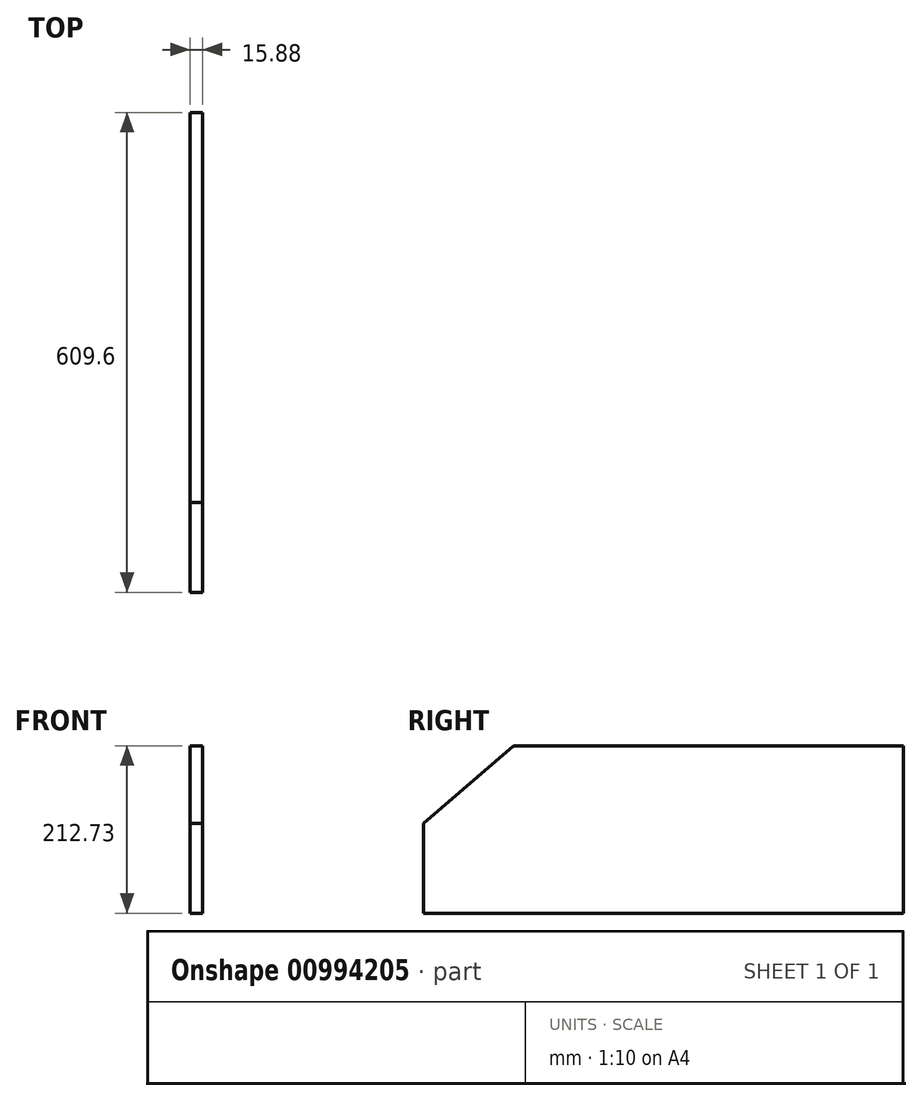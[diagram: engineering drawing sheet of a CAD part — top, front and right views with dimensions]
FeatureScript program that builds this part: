
annotation { "Feature Type Name" : "Feature", "Feature Type Description" : "" }
export const myFeature = defineFeature(function(context is Context, id is Id, definition is map)
    precondition{}
    {
        {
            var Q0;
            Q0=qCreatedBy(makeId("Right.planeOp"),FACE);
            var sketch = newSketch(context, id + "F0", { "sketchPlane" : qUnion([Q0])});
            skLineSegment(sketch, "E0", {"start": v(0.04, 0.07) * mm, "end": v(609.64, 0.07) * mm});
            skLineSegment(sketch, "E1", {"start": v(609.64, 0.07) * mm, "end": v(609.64, 212.8) * mm});
            skLineSegment(sketch, "E2", {"start": v(609.64, 212.8) * mm, "end": v(114.34, 212.8) * mm});
            skLineSegment(sketch, "E3", {"start": v(114.34, 212.8) * mm, "end": v(0.04, 114.37) * mm});
            skLineSegment(sketch, "E4", {"start": v(0.04, 114.37) * mm, "end": v(0.04, 0.07) * mm});
            skSolve(sketch);
        }
        {
            var Q0;
            Q0=makeQuery(id+"F0.imprint","IMPRINT",FACE,{"disambiguationData":[TD([[makeQuery(id+"F0.imprint","IMPRINT",EDGE,{"derivedFrom":sQuery(id+"F0.wireOp",EDGE,"E0")}),1.0]])]});
            extrude(context, id + "F1", {"entities" : qUnion([Q0]), "depth" : 15.88 * mm, "offsetDistance" : 25.4 * mm});
        }
    });
